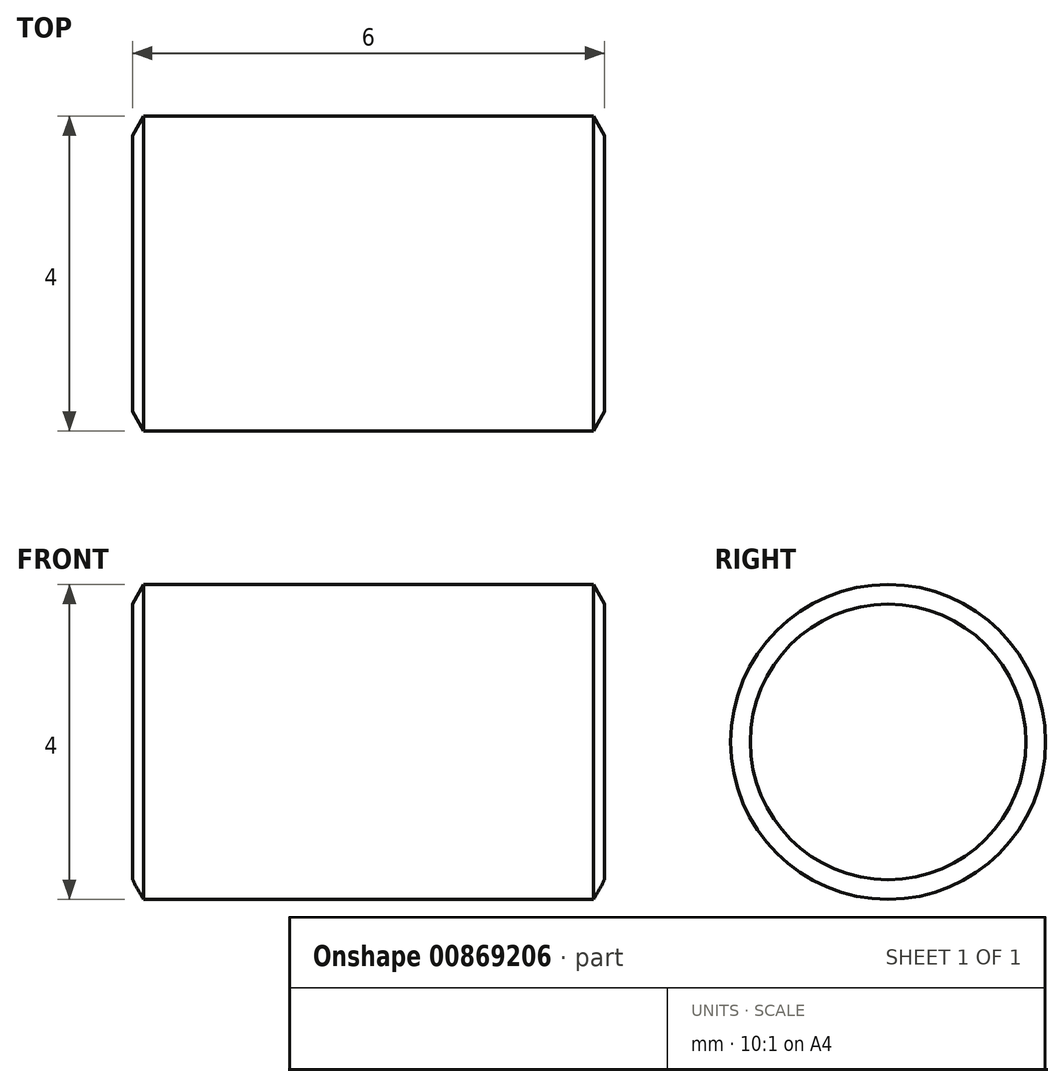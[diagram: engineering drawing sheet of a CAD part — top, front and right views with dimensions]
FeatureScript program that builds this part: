
annotation { "Feature Type Name" : "Feature", "Feature Type Description" : "" }
export const myFeature = defineFeature(function(context is Context, id is Id, definition is map)
    precondition{}
    {
        {
            var Q0;
            Q0=qCreatedBy(makeId("Right.planeOp"),FACE);
            var sketch = newSketch(context, id + "F0", { "sketchPlane" : qUnion([Q0])});
            skCircle(sketch, "E0", {"center": v(0, 0) * mm, "radius": 2 * mm});
            skSolve(sketch);
        }
        {
            var Q0;
            Q0=makeQuery(id+"F0.imprint","IMPRINT",FACE,{"disambiguationData":[TD([[makeQuery(id+"F0.imprint","IMPRINT",EDGE,{"derivedFrom":sQuery(id+"F0.wireOp",EDGE,"E0")}),1.0]])]});
            extrude(context, id + "F1", {"entities" : qUnion([Q0]), "depth" : (6) * mm, "offsetDistance" : 25 * mm});
        }
        {
            var Q0;
            Q0=makeQuery(id+"F1.opExtrude","CAP_EDGE",EDGE,{"disambiguationData":[OSD([sQuery(id+"F0.wireOp",EDGE,"E0")])],"isStart":false});
            var Q1;
            Q1=makeQuery(id+"F1.opExtrude","CAP_EDGE",EDGE,{"disambiguationData":[OSD([sQuery(id+"F0.wireOp",EDGE,"E0")])],"isStart":true});
            chamfer(context, id + "F2", {"entities" : qUnion([Q0, Q1]), "chamferType" : ChamferType.OFFSET_ANGLE, "width" : .25 * mm, "oppositeDirection" : true, "angle" : 30 * degree, "tangentPropagation" : true});
        }
    });
